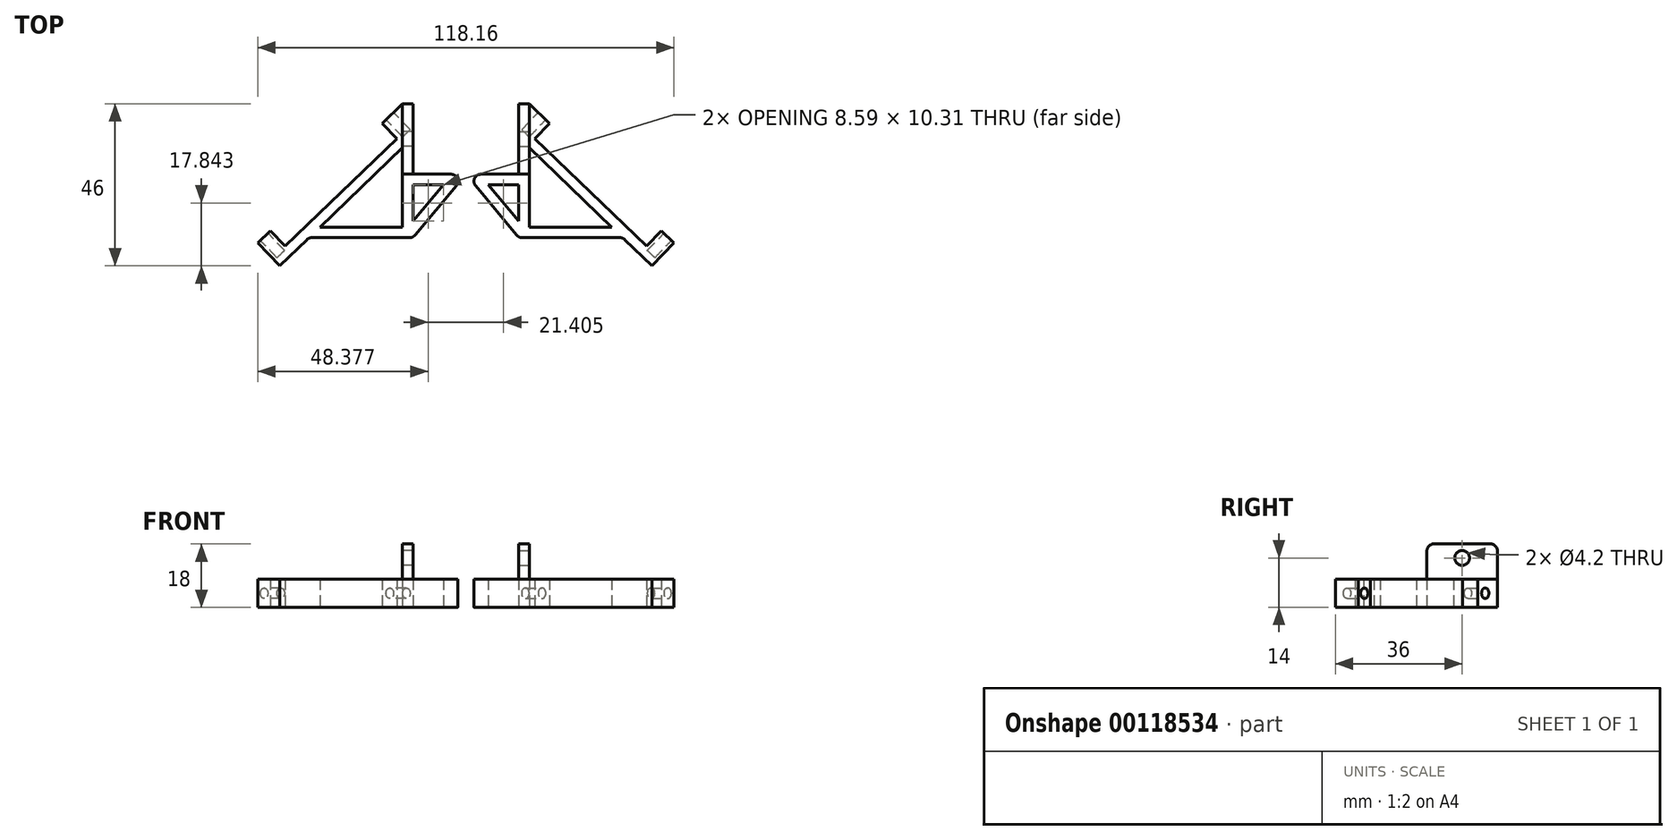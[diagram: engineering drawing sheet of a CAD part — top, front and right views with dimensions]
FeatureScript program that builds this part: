
annotation { "Feature Type Name" : "Feature", "Feature Type Description" : "" }
export const myFeature = defineFeature(function(context is Context, id is Id, definition is map)
    precondition{}
    {
        {
            var Q0;
            Q0=qCreatedBy(makeId("Top.planeOp"),FACE);
            var sketch = newSketch(context, id + "F0", { "sketchPlane" : qUnion([Q0])});
            skLineSegment(sketch, "E0", {"start": v(-18, 20) * mm, "end": v(-18, -18) * mm});
            skLineSegment(sketch, "E1", {"start": v(-18, -18) * mm, "end": v(-15, -18) * mm});
            skLineSegment(sketch, "E2", {"start": v(-15, -18) * mm, "end": v(-15, 20) * mm});
            skLineSegment(sketch, "E3", {"start": v(-15, 20) * mm, "end": v(-18, 20) * mm});
            skLineSegment(sketch, "E4", {"start": v(-15, -3) * mm, "end": v(-6.4, -3) * mm});
            skLineSegment(sketch, "E5", {"start": v(-6.4, -3) * mm, "end": v(-15, -13.31) * mm});
            skLineSegment(sketch, "E6", {"start": v(-15, -18) * mm, "end": v(0, 0) * mm});
            skLineSegment(sketch, "E7", {"start": v(0, 0) * mm, "end": v(-15, 0) * mm});
            skLineSegment(sketch, "E8", {"start": v(-18, 11.68) * mm, "end": v(-54.92, -23.84) * mm});
            skLineSegment(sketch, "E9", {"start": v(-54.92, -23.84) * mm, "end": v(-52.84, -26) * mm});
            skLineSegment(sketch, "E10", {"start": v(-52.84, -26) * mm, "end": v(-18, 7.51) * mm});
            skLineSegment(sketch, "E11", {"start": v(-18, -15) * mm, "end": v(-41.4, -15) * mm});
            skLineSegment(sketch, "E12", {"start": v(-41.4, -15) * mm, "end": v(-44.53, -18) * mm});
            skLineSegment(sketch, "E13", {"start": v(-44.53, -18) * mm, "end": v(-18, -18) * mm});
            skLineSegment(sketch, "E14", {"start": v(-54.92, -23.84) * mm, "end": v(-59.08, -19.51) * mm});
            skLineSegment(sketch, "E15", {"start": v(-59.08, -19.51) * mm, "end": v(-55.48, -16.05) * mm});
            skLineSegment(sketch, "E16", {"start": v(-55.48, -16.05) * mm, "end": v(-51.32, -20.37) * mm});
            skLineSegment(sketch, "E17", {"start": v(-19.6, 10.13) * mm, "end": v(-23.77, 14.45) * mm});
            skLineSegment(sketch, "E18", {"start": v(-23.77, 14.45) * mm, "end": v(-18, 20) * mm});
            skSolve(sketch);
        }
        {
            var Q0;
            Q0 = qSketchRegion(id + "F0", true);
            extrude(context, id + "F1", {"entities" : qUnion([Q0]), "depth" : 8 * mm});
        }
        {
            var Q0;
            Q0=makeQuery(id+"F1.opExtrude","SWEPT_FACE",FACE,{"disambiguationData":[OSD([sQuery(id+"F0.wireOp",EDGE,"E15")])]});
            var sketch = newSketch(context, id + "F2", { "sketchPlane" : qUnion([Q0])});
            skLineSegment(sketch, "E19", {"start": v(56.1, 4) * mm, "end": v(0, 4) * mm, "construction": true});
            skCircle(sketch, "E20", {"center": v(53.6, 4) * mm, "radius": 1.5 * mm});
            skCircle(sketch, "E21", {"center": v(4.1, 4) * mm, "radius": 1.5 * mm});
            skSolve(sketch);
        }
        {
            var Q0;
            Q0 = qSketchRegion(id + "F2", true);
            extrude(context, id + "F3", {"entities" : qUnion([Q0]), "operationType" : NewBodyOperationType.REMOVE, "oppositeDirection" : true, "depth" : 6.8 * mm});
        }
        {
            var Q0;
            Q0=makeQuery(id+"F1.opExtrude","CAP_FACE",FACE,{"disambiguationData":[OSD([sQuery(id+"F0.wireOp",EDGE,"E0"),sQuery(id+"F0.wireOp",EDGE,"E1"),sQuery(id+"F0.wireOp",EDGE,"E2"),sQuery(id+"F0.wireOp",EDGE,"E3"),sQuery(id+"F0.wireOp",EDGE,"E4"),sQuery(id+"F0.wireOp",EDGE,"E5"),sQuery(id+"F0.wireOp",EDGE,"E6"),sQuery(id+"F0.wireOp",EDGE,"E7"),sQuery(id+"F0.wireOp",EDGE,"E8"),sQuery(id+"F0.wireOp",EDGE,"E9"),sQuery(id+"F0.wireOp",EDGE,"E10"),sQuery(id+"F0.wireOp",EDGE,"E11"),sQuery(id+"F0.wireOp",EDGE,"E13"),sQuery(id+"F0.wireOp",EDGE,"E14"),sQuery(id+"F0.wireOp",EDGE,"E15"),sQuery(id+"F0.wireOp",EDGE,"E16"),sQuery(id+"F0.wireOp",EDGE,"E17"),sQuery(id+"F0.wireOp",EDGE,"E18")])],"isStart":false});
            var sketch = newSketch(context, id + "F4", { "sketchPlane" : qUnion([Q0])});
            skLineSegment(sketch, "E22", {"start": v(-15, 0) * mm, "end": v(-15, 20) * mm});
            skLineSegment(sketch, "E23", {"start": v(-15, 20) * mm, "end": v(-18, 20) * mm});
            skLineSegment(sketch, "E24", {"start": v(-18, 20) * mm, "end": v(-18, 0) * mm});
            skLineSegment(sketch, "E25", {"start": v(-18, 0) * mm, "end": v(-15, 0) * mm});
            skSolve(sketch);
        }
        {
            var Q0;
            Q0 = qSketchRegion(id + "F4", true);
            extrude(context, id + "F5", {"entities" : qUnion([Q0]), "operationType" : NewBodyOperationType.ADD, "depth" : 10 * mm});
        }
        {
            var Q0;
            Q0=makeQuery(id+"F1.opExtrude","SWEPT_EDGE",EDGE,{"disambiguationData":[OSD([sQuery(id+"F0.wireOp",EDGE,"E6"),sQuery(id+"F0.wireOp",EDGE,"E7")])]});
            var Q1;
            Q1=makeQuery(id+"F1.opExtrude","SWEPT_EDGE",EDGE,{"disambiguationData":[OSD([sQuery(id+"F0.wireOp",EDGE,"E1"),sQuery(id+"F0.wireOp",EDGE,"E2"),sQuery(id+"F0.wireOp",EDGE,"E6")])]});
            var Q2;
            Q2=makeQuery(id+"F1.opExtrude","SWEPT_EDGE",EDGE,{"disambiguationData":[OSD([sQuery(id+"F0.wireOp",EDGE,"E10"),sQuery(id+"F0.wireOp",EDGE,"E12"),sQuery(id+"F0.wireOp",EDGE,"E13")])]});
            var Q3;
            Q3=makeQuery(id+"F5.opExtrude","CAP_EDGE",EDGE,{"disambiguationData":[OSD([sQuery(id+"F4.wireOp",EDGE,"E25")])],"isStart":false});
            var Q4;
            Q4=makeQuery(id+"F5.opExtrude","CAP_EDGE",EDGE,{"disambiguationData":[OSD([sQuery(id+"F4.wireOp",EDGE,"E23")])],"isStart":false});
            fillet(context, id + "F6", {"entities" : qUnion([Q0, Q1, Q2, Q3, Q4]), "radius" : 2 * mm, "tangentPropagation" : true, "allowEdgeOverflow" : false});
        }
        {
            var Q0;
            Q0=makeQuery(id+"F5.boolean.opBoolean","MERGE",FACE,{"derivedFrom":[makeQuery(id+"F1.opExtrude","SWEPT_FACE",FACE,{"disambiguationData":[OSD([sQuery(id+"F0.wireOp",EDGE,"E0")])]}),makeQuery(id+"F5.opExtrude","SWEPT_FACE",FACE,{"disambiguationData":[OSD([sQuery(id+"F4.wireOp",EDGE,"E24")])]})]});
            var sketch = newSketch(context, id + "F7", { "sketchPlane" : qUnion([Q0])});
            skLineSegment(sketch, "E26", {"start": v(-10, 18) * mm, "end": v(-10, 8) * mm, "construction": true});
            skCircle(sketch, "E27", {"center": v(-10, 14) * mm, "radius": 2.1 * mm});
            skSolve(sketch);
        }
        {
            var Q0;
            Q0 = qSketchRegion(id + "F7", true);
            extrude(context, id + "F8", {"entities" : qUnion([Q0]), "operationType" : NewBodyOperationType.REMOVE, "endBound" : BoundingType.THROUGH_ALL, "oppositeDirection" : true, "depth" : 25 * mm});
        }
        {
            var Q0;
            Q0=makeQuery(id+"F1.opExtrude","SWEPT_BODY",BODY,{"disambiguationData":[OSD([sQuery(id+"F0.wireOp",EDGE,"E0"),sQuery(id+"F0.wireOp",EDGE,"E1"),sQuery(id+"F0.wireOp",EDGE,"E2"),sQuery(id+"F0.wireOp",EDGE,"E3"),sQuery(id+"F0.wireOp",EDGE,"E4"),sQuery(id+"F0.wireOp",EDGE,"E5"),sQuery(id+"F0.wireOp",EDGE,"E6"),sQuery(id+"F0.wireOp",EDGE,"E7"),sQuery(id+"F0.wireOp",EDGE,"E8"),sQuery(id+"F0.wireOp",EDGE,"E9"),sQuery(id+"F0.wireOp",EDGE,"E10"),sQuery(id+"F0.wireOp",EDGE,"E11"),sQuery(id+"F0.wireOp",EDGE,"E13"),sQuery(id+"F0.wireOp",EDGE,"E14"),sQuery(id+"F0.wireOp",EDGE,"E15"),sQuery(id+"F0.wireOp",EDGE,"E16"),sQuery(id+"F0.wireOp",EDGE,"E17"),sQuery(id+"F0.wireOp",EDGE,"E18")])]});
            var Q1;
            Q1=qCreatedBy(makeId("Right.planeOp"),FACE);
            mirror(context, id + "F9", {"entities" : qUnion([Q0]), "mirrorPlane" : qUnion([Q1])});
        }
    });
